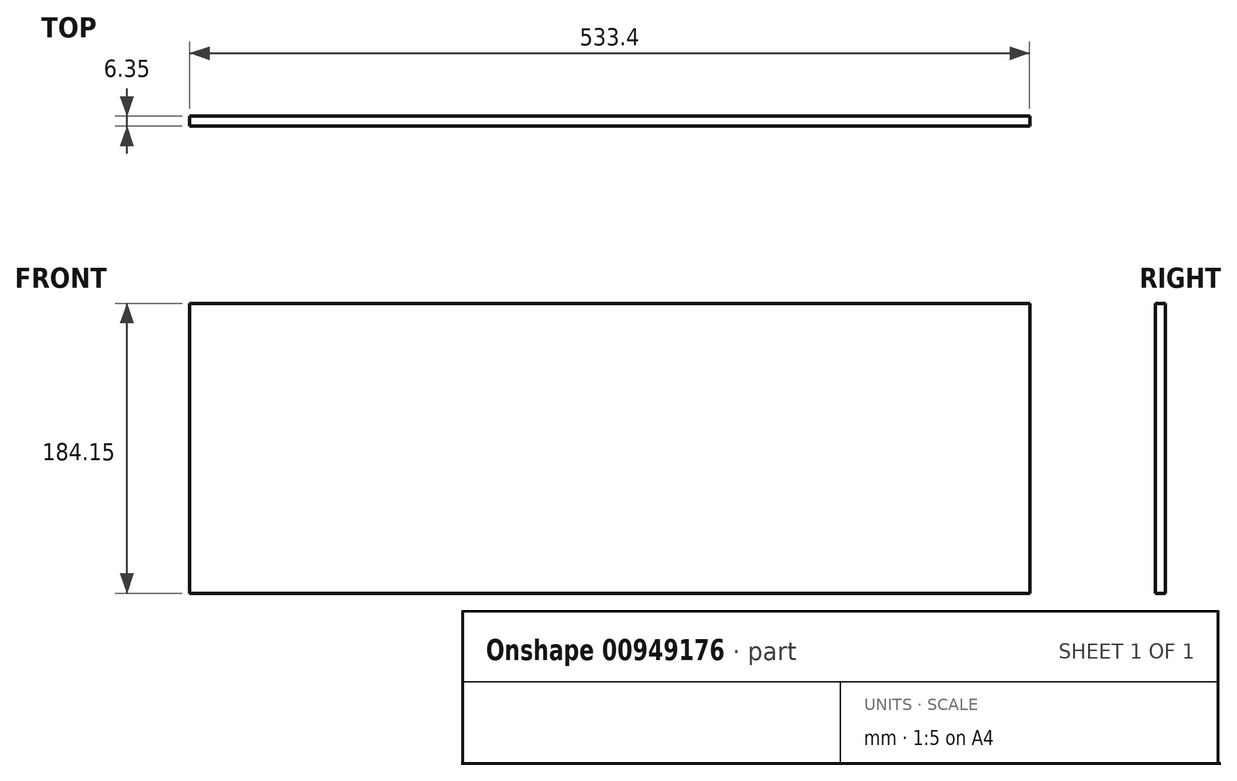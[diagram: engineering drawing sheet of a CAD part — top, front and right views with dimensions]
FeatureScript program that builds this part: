
annotation { "Feature Type Name" : "Feature", "Feature Type Description" : "" }
export const myFeature = defineFeature(function(context is Context, id is Id, definition is map)
    precondition{}
    {
        {
            var Q0;
            Q0=qCreatedBy(makeId("Front.planeOp"),FACE);
            var sketch = newSketch(context, id + "F0", { "sketchPlane" : qUnion([Q0])});
            skLineSegment(sketch, "E0.bottom", {"start": v(-290.57, 70.38) * mm, "end": v(242.83, 70.38) * mm});
            skLineSegment(sketch, "E0.top", {"start": v(-290.57, -113.77) * mm, "end": v(242.83, -113.77) * mm});
            skLineSegment(sketch, "E0.left", {"start": v(-290.57, 70.38) * mm, "end": v(-290.57, -113.77) * mm});
            skLineSegment(sketch, "E0.right", {"start": v(242.83, 70.38) * mm, "end": v(242.83, -113.77) * mm});
            skSolve(sketch);
        }
        {
            var Q0;
            Q0=makeQuery(id+"F0.imprint","IMPRINT",FACE,{"disambiguationData":[TD([[makeQuery(id+"F0.imprint","IMPRINT",EDGE,{"derivedFrom":sQuery(id+"F0.wireOp",EDGE,"E0.bottom")}),-1.0]])]});
            extrude(context, id + "F1", {"entities" : qUnion([Q0]), "depth" : 6.35 * mm, "offsetDistance" : 25.4 * mm});
        }
    });
